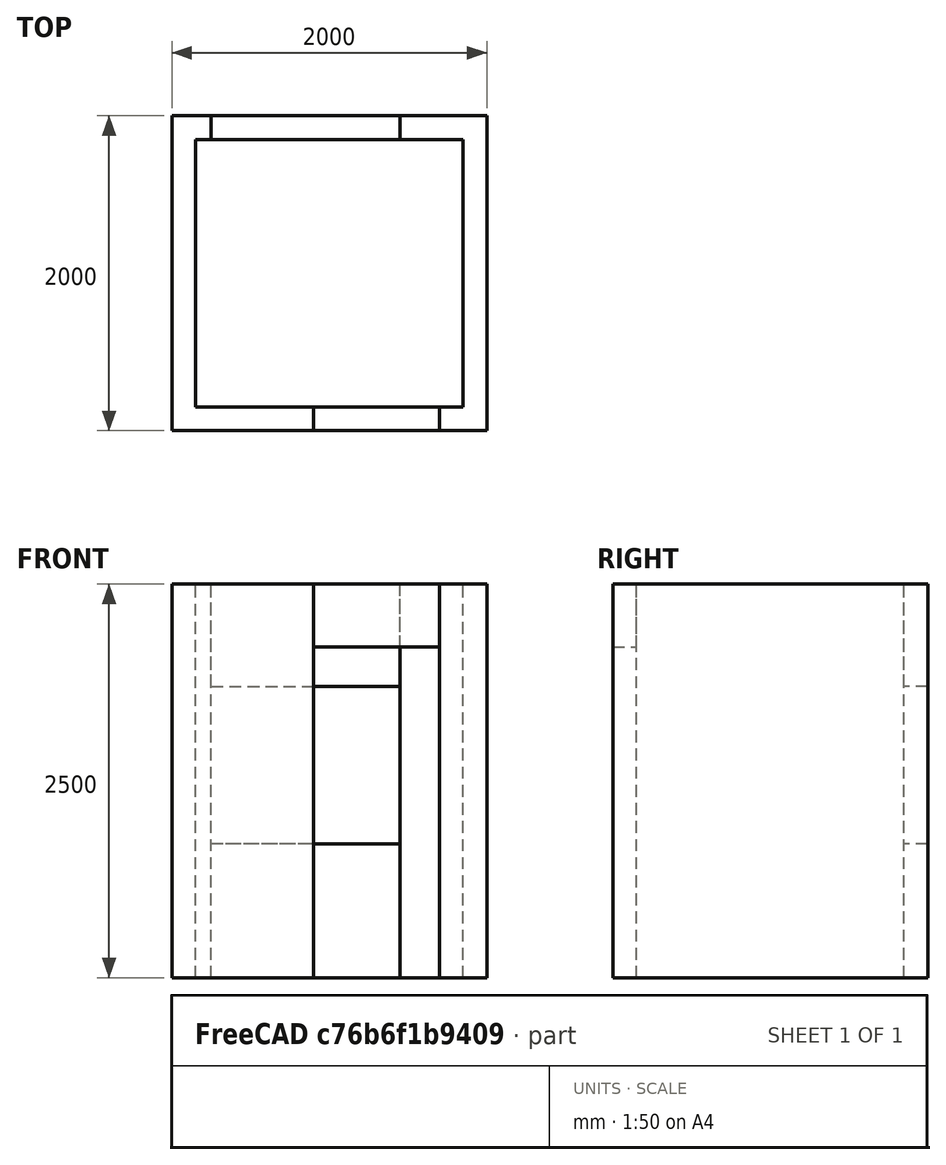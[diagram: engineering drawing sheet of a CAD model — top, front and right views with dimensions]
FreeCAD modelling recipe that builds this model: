
FCSTD DOCUMENT  (FreeCAD 0.17R13519 (Git))
Label: test007_draft
License: All rights reserved
LicenseURL: http://en.wikipedia.org/wiki/All_rights_reserved
objects: Part::Feature×80, Part::Part2DObjectPython×23, App::FeaturePython×10, App::DocumentObjectGroup×8, Part::Extrusion×7, Part::Cut×2
note: 112 computed .brp shape members not serialized (recipe doc carries the construction recipe); baked Part::Feature solids carry a one-line shape summary decoded from their .brp

FEATURE [Part::Part2DObjectPython] Rectangle  # Draft 2D object (typed FeaturePython)
  ChamferSize = 0
  Columns = 1
  FilletRadius = 0
  Height = 2000
  Length = 2000
  MakeFace = false
  Rows = 1
FEATURE [Part::Part2DObjectPython] Rectangle001  # Draft 2D object (typed FeaturePython)
  ChamferSize = 0
  Columns = 1
  FilletRadius = 0
  Height = 1700
  Length = 1700
  MakeFace = false
  Placement = pos=(150,150,0) rot=(0,0,1;0rad)
  Rows = 1
FEATURE [Part::Part2DObjectPython] Line  # Draft 2D object (typed FeaturePython)
  ChamferSize = 0
  Closed = false
  End = (150,3000,0)
  FilletRadius = 0
  Length = 2000
  MakeFace = true
  Points = (2) [(150,1000,0),(150,3000,0)]
  Start = (150,1000,0)
  Subdivisions = 0
FEATURE [Part::Part2DObjectPython] Line001  # Draft 2D object (typed FeaturePython)
  ChamferSize = 0
  Closed = false
  End = (250,3000,0)
  FilletRadius = 0
  Length = 2000
  MakeFace = true
  Placement = pos=(100,0,0) rot=(0,0,1;0rad)
  Points = (2) [(150,1000,0),(150,3000,0)]
  Start = (250,1000,0)
  Subdivisions = 0
FEATURE [Part::Part2DObjectPython] Line002  # Draft 2D object (typed FeaturePython)
  ChamferSize = 0
  Closed = false
  End = (1450,3000,0)
  FilletRadius = 0
  Length = 2000
  MakeFace = true
  Placement = pos=(1300,0,0) rot=(0,0,1;0rad)
  Points = (2) [(150,1000,0),(150,3000,0)]
  Start = (1450,1000,0)
  Subdivisions = 0
FEATURE [Part::Part2DObjectPython] Line003  # Draft 2D object (typed FeaturePython)
  ChamferSize = 0
  Closed = false
  End = (900,1000,0)
  FilletRadius = 0
  Length = 2000
  MakeFace = true
  Placement = pos=(750,-2000,0) rot=(0,0,1;0rad)
  Points = (2) [(150,1000,0),(150,3000,0)]
  Start = (900,-1000,0)
  Subdivisions = 0
FEATURE [Part::Part2DObjectPython] Line004  # Draft 2D object (typed FeaturePython)
  ChamferSize = 0
  Closed = false
  End = (1700,1000,0)
  FilletRadius = 0
  Length = 2000
  MakeFace = true
  Placement = pos=(1550,-2000,0) rot=(0,0,1;0rad)
  Points = (2) [(150,1000,0),(150,3000,0)]
  Start = (1700,-1000,0)
  Subdivisions = 0
FEATURE [Part::Part2DObjectPython] Line005  # Draft 2D object (typed FeaturePython)
  ChamferSize = 0
  Closed = false
  End = (1850,1000,0)
  FilletRadius = 0
  Length = 2000
  MakeFace = true
  Placement = pos=(1700,-2000,0) rot=(0,0,1;0rad)
  Points = (2) [(150,1000,0),(150,3000,0)]
  Start = (1850,-1000,0)
  Subdivisions = 0
FEATURE [Part::Part2DObjectPython] DWire  # Draft 2D object (typed FeaturePython)
  ChamferSize = 0
  Closed = true
  End = (250,2000,0)
  FilletRadius = 0
  Length = 6000
  MakeFace = true
  Points = (8) [(250,1850,0),(150,1850,0),(150,150,0),(900,150,0),(900,2.75546e-14,0),(1.26218e-29,3.8643e-46,0),(-6.12323e-14,2000,0),(250,2000,0)]
  Start = (250,1850,0)
  Subdivisions = 0
FEATURE [Part::Part2DObjectPython] DWire001  # Draft 2D object (typed FeaturePython)
  ChamferSize = 0
  Closed = true
  End = (1850,150,0)
  FilletRadius = 0
  Length = 5400
  MakeFace = true
  Points = (8) [(1700,150,0),(1700,0,0),(2000,6.1e-14,0),(2000,2000,0),(1450,2000,0),(1450,1850,0),(1850,1850,0),(1850,150,0)]
  Start = (1700,150,0)
  Subdivisions = 0
FEATURE [Part::Part2DObjectPython] Line006  # Draft 2D object (typed FeaturePython)
  ChamferSize = 0
  Closed = false
  End = (1450,1925,0)
  FilletRadius = 0
  Length = 1200
  MakeFace = false
  Points = (2) [(250,1925,0),(1450,1925,0)]
  Start = (250,1925,0)
  Subdivisions = 0
FEATURE [Part::Part2DObjectPython] Line009  # Draft 2D object (typed FeaturePython)
  ChamferSize = 0
  Closed = false
  End = (250,2000,0)
  FilletRadius = 0
  Length = 1200
  MakeFace = false
  Points = (2) [(1450,2000,0),(250,2000,0)]
  Start = (1450,2000,0)
  Subdivisions = 0
FEATURE [Part::Part2DObjectPython] Line011  # Draft 2D object (typed FeaturePython)
  ChamferSize = 0
  Closed = false
  End = (1450,1850,0)
  FilletRadius = 0
  Length = 1200
  MakeFace = false
  Points = (2) [(250,1850,0),(1450,1850,0)]
  Start = (250,1850,0)
  Subdivisions = 0
FEATURE [Part::Part2DObjectPython] Line013  # Draft 2D object (typed FeaturePython)
  ChamferSize = 0
  Closed = false
  End = (1700,150,0)
  FilletRadius = 0
  Length = 800
  MakeFace = false
  Points = (2) [(900,150,0),(1700,150,0)]
  Start = (900,150,0)
  Subdivisions = 0
FEATURE [Part::Part2DObjectPython] Line015  # Draft 2D object (typed FeaturePython)
  ChamferSize = 0
  Closed = false
  End = (1695.52,871.443,0)
  FilletRadius = 0
  Length = 800
  MakeFace = false
  Placement = pos=(1620.52,1771.44,0) rot=(0,0,-1;1.5708rad)
  Points = (2) [(1700,75,0),(900,75,0)]
  Start = (1695.52,71.4434,0)
  Subdivisions = 0
FEATURE [Part::Part2DObjectPython] Line019  # Draft 2D object (typed FeaturePython)
  ChamferSize = 0
  Closed = false
  End = (900,0,0)
  FilletRadius = 0
  Length = 800
  MakeFace = false
  Points = (2) [(1700,0,0),(900,2.8e-14,0)]
  Start = (1700,0,0)
  Subdivisions = 0
FEATURE [Part::Part2DObjectPython] Arc  # Draft 2D object (typed FeaturePython)
  FirstAngle = 90.3221
  LastAngle = 174.435
  MakeFace = false
  Placement = pos=(1700,75,0) rot=(0,0,1;0rad)
  Radius = 796.456
FEATURE [Part::Part2DObjectPython] Rectangle002  # Draft 2D object (typed FeaturePython)
  ChamferSize = 0
  Columns = 1
  FilletRadius = 0
  Height = 600
  Length = 1700
  MakeFace = false
  Placement = pos=(150,1250,800) rot=(0,0,1;0rad)
  Rows = 1
FEATURE [Part::Feature] Shape
  Placement = pos=(-6227.42,-15812.2,800) rot=(0,0,1;0rad)
  shape: bbox 182.6 x 182.6 x 2e-07 mm, 0 faces, 0 solids (baked)
FEATURE [Part::Feature] Shape001
  Placement = pos=(-6227.42,-15812.2,800) rot=(0,0,1;0rad)
  shape: bbox 2e-07 x 40.64 x 2e-07 mm, 0 faces, 0 solids (baked)
FEATURE [Part::Feature] Shape002
  Placement = pos=(-6227.42,-15812.2,800) rot=(0,0,1;0rad)
  shape: bbox 162.6 x 162.6 x 2e-07 mm, 0 faces, 0 solids (baked)
FEATURE [Part::Feature] Shape003
  Placement = pos=(-6227.42,-15812.2,800) rot=(0,0,1;0rad)
  shape: bbox 2e-07 x 600 x 2e-07 mm, 0 faces, 0 solids (baked)
FEATURE [Part::Feature] Shape004
  Placement = pos=(-6227.42,-15812.2,800) rot=(0,0,1;0rad)
  shape: bbox 2e-07 x 600 x 2e-07 mm, 0 faces, 0 solids (baked)
FEATURE [Part::Feature] Shape005
  Placement = pos=(-6227.42,-15812.2,800) rot=(0,0,1;0rad)
  shape: bbox 2e-07 x 600 x 2e-07 mm, 0 faces, 0 solids (baked)
FEATURE [Part::Feature] Shape006
  Placement = pos=(-6227.42,-15812.2,800) rot=(0,0,1;0rad)
  shape: bbox 150 x 150 x 2e-07 mm, 0 faces, 0 solids (baked)
FEATURE [Part::Feature] Shape007
  Placement = pos=(-6227.42,-15812.2,800) rot=(0,0,1;0rad)
  shape: bbox 182.6 x 182.6 x 2e-07 mm, 0 faces, 0 solids (baked)
FEATURE [Part::Feature] Shape008
  Placement = pos=(-6227.42,-15812.2,800) rot=(0,0,1;0rad)
  shape: bbox 2e-07 x 32.51 x 2e-07 mm, 0 faces, 0 solids (baked)
FEATURE [Part::Feature] Shape009
  Placement = pos=(-6227.42,-15812.2,800) rot=(0,0,1;0rad)
  shape: bbox 2e-07 x 40.64 x 2e-07 mm, 0 faces, 0 solids (baked)
FEATURE [Part::Feature] Shape010
  Placement = pos=(-6227.42,-15812.2,800) rot=(0,0,1;0rad)
  shape: bbox 32.51 x 2e-07 x 2e-07 mm, 0 faces, 0 solids (baked)
FEATURE [Part::Feature] Shape011
  Placement = pos=(-6227.42,-15812.2,800) rot=(0,0,1;0rad)
  shape: bbox 40.64 x 2e-07 x 2e-07 mm, 0 faces, 0 solids (baked)
FEATURE [Part::Feature] Shape012
  Placement = pos=(-6227.42,-15812.2,800) rot=(0,0,1;0rad)
  shape: bbox 40.64 x 2e-07 x 2e-07 mm, 0 faces, 0 solids (baked)
FEATURE [Part::Feature] Shape013
  Placement = pos=(-6227.42,-15812.2,800) rot=(0,0,1;0rad)
  shape: bbox 130 x 130 x 2e-07 mm, 0 faces, 0 solids (baked)
FEATURE [Part::Feature] Shape014
  Placement = pos=(-6227.42,-15812.2,800) rot=(0,0,1;0rad)
  shape: bbox 2e-07 x 32.51 x 2e-07 mm, 0 faces, 0 solids (baked)
FEATURE [Part::Feature] Shape015
  Placement = pos=(-6227.42,-15812.2,800) rot=(0,0,1;0rad)
  shape: bbox 32.51 x 2e-07 x 2e-07 mm, 0 faces, 0 solids (baked)
FEATURE [Part::Feature] Shape016
  Placement = pos=(-6227.42,-15812.2,800) rot=(0,0,1;0rad)
  shape: bbox 162.6 x 162.6 x 2e-07 mm, 0 faces, 0 solids (baked)
FEATURE [Part::Feature] Shape017
  Placement = pos=(-6227.42,-15812.2,800) rot=(0,0,1;0rad)
  shape: bbox 2e-07 x 40.64 x 2e-07 mm, 0 faces, 0 solids (baked)
FEATURE [Part::Feature] Shape018
  Placement = pos=(-6227.42,-15812.2,800) rot=(0,0,1;0rad)
  shape: bbox 500 x 2e-07 x 2e-07 mm, 0 faces, 0 solids (baked)
FEATURE [Part::Feature] Shape019
  Placement = pos=(-6227.42,-15812.2,800) rot=(0,0,1;0rad)
  shape: bbox 150 x 150 x 2e-07 mm, 0 faces, 0 solids (baked)
FEATURE [Part::Feature] Shape020 .. Shape023  x4 (patterned run collapsed; names and placements below)
  shape: bbox 41.11 x 41.11 x 2e-07 mm, 0 faces, 0 solids (baked)
  placements: all 4 at pos=(-6227.42,-15812.2,800) rot=(0,0,1;0rad)
FEATURE [Part::Feature] Shape024
  Placement = pos=(-6227.42,-15812.2,800) rot=(0,0,1;0rad)
  shape: bbox 21.21 x 21.21 x 2e-07 mm, 0 faces, 0 solids (baked)
FEATURE [Part::Feature] Shape025
  Placement = pos=(-6227.42,-15812.2,800) rot=(0,0,1;0rad)
  shape: bbox 5.657 x 5.657 x 2e-07 mm, 0 faces, 0 solids (baked)
FEATURE [Part::Feature] Shape026
  Placement = pos=(-6227.42,-15812.2,800) rot=(0,0,1;0rad)
  shape: bbox 21.21 x 21.21 x 2e-07 mm, 0 faces, 0 solids (baked)
FEATURE [Part::Feature] Shape027
  Placement = pos=(-6227.42,-15812.2,800) rot=(0,0,1;0rad)
  shape: bbox 5.657 x 5.657 x 2e-07 mm, 0 faces, 0 solids (baked)
FEATURE [Part::Feature] Shape028
  Placement = pos=(-6227.42,-15812.2,800) rot=(0,0,1;0rad)
  shape: bbox 21.21 x 21.21 x 2e-07 mm, 0 faces, 0 solids (baked)
FEATURE [Part::Feature] Shape029
  Placement = pos=(-6227.42,-15812.2,800) rot=(0,0,1;0rad)
  shape: bbox 5.657 x 5.657 x 2e-07 mm, 0 faces, 0 solids (baked)
FEATURE [Part::Feature] Shape030
  Placement = pos=(-6227.42,-15812.2,800) rot=(0,0,1;0rad)
  shape: bbox 21.21 x 21.21 x 2e-07 mm, 0 faces, 0 solids (baked)
FEATURE [Part::Feature] Shape031
  Placement = pos=(-6227.42,-15812.2,800) rot=(0,0,1;0rad)
  shape: bbox 5.657 x 5.657 x 2e-07 mm, 0 faces, 0 solids (baked)
FEATURE [Part::Feature] Shape032
  Placement = pos=(-6227.42,-15812.2,800) rot=(0,0,1;0rad)
  shape: bbox 21.21 x 21.21 x 2e-07 mm, 0 faces, 0 solids (baked)
FEATURE [Part::Feature] Shape033
  Placement = pos=(-6227.42,-15812.2,800) rot=(0,0,1;0rad)
  shape: bbox 5.657 x 5.657 x 2e-07 mm, 0 faces, 0 solids (baked)
FEATURE [Part::Feature] Shape034
  Placement = pos=(-6227.42,-15812.2,800) rot=(0,0,1;0rad)
  shape: bbox 21.21 x 21.21 x 2e-07 mm, 0 faces, 0 solids (baked)
FEATURE [Part::Feature] Shape035
  Placement = pos=(-6227.42,-15812.2,800) rot=(0,0,1;0rad)
  shape: bbox 5.657 x 5.657 x 2e-07 mm, 0 faces, 0 solids (baked)
FEATURE [Part::Feature] Shape036
  Placement = pos=(-6227.42,-15812.2,800) rot=(0,0,1;0rad)
  shape: bbox 21.21 x 21.21 x 2e-07 mm, 0 faces, 0 solids (baked)
FEATURE [Part::Feature] Shape037
  Placement = pos=(-6227.42,-15812.2,800) rot=(0,0,1;0rad)
  shape: bbox 5.657 x 5.657 x 2e-07 mm, 0 faces, 0 solids (baked)
FEATURE [Part::Feature] Shape038
  Placement = pos=(-6227.42,-15812.2,800) rot=(0,0,1;0rad)
  shape: bbox 21.21 x 21.21 x 2e-07 mm, 0 faces, 0 solids (baked)
FEATURE [Part::Feature] Shape039
  Placement = pos=(-6227.42,-15812.2,800) rot=(0,0,1;0rad)
  shape: bbox 5.657 x 5.657 x 2e-07 mm, 0 faces, 0 solids (baked)
FEATURE [Part::Feature] Shape040
  Placement = pos=(-6227.42,-15812.2,800) rot=(0,0,1;0rad)
  shape: bbox 500 x 2e-07 x 2e-07 mm, 0 faces, 0 solids (baked)
FEATURE [Part::Feature] Shape041
  Placement = pos=(-6227.42,-15812.2,800) rot=(0,0,1;0rad)
  shape: bbox 40.64 x 2e-07 x 2e-07 mm, 0 faces, 0 solids (baked)
FEATURE [Part::Feature] Shape042
  Placement = pos=(-6227.42,-15812.2,800) rot=(0,0,1;0rad)
  shape: bbox 40.64 x 2e-07 x 2e-07 mm, 0 faces, 0 solids (baked)
FEATURE [Part::Feature] Shape043
  Placement = pos=(-6227.42,-15812.2,800) rot=(0,0,1;0rad)
  shape: bbox 32.51 x 2e-07 x 2e-07 mm, 0 faces, 0 solids (baked)
FEATURE [Part::Feature] Shape044
  Placement = pos=(-6227.42,-15812.2,800) rot=(0,0,1;0rad)
  shape: bbox 2e-07 x 32.51 x 2e-07 mm, 0 faces, 0 solids (baked)
FEATURE [Part::Feature] Shape045
  Placement = pos=(-6227.42,-15812.2,800) rot=(0,0,1;0rad)
  shape: bbox 32.51 x 2e-07 x 2e-07 mm, 0 faces, 0 solids (baked)
FEATURE [Part::Feature] Shape046
  Placement = pos=(-6227.42,-15812.2,800) rot=(0,0,1;0rad)
  shape: bbox 2e-07 x 40.64 x 2e-07 mm, 0 faces, 0 solids (baked)
FEATURE [Part::Feature] Shape047
  Placement = pos=(-6227.42,-15812.2,800) rot=(0,0,1;0rad)
  shape: bbox 130 x 130 x 2e-07 mm, 0 faces, 0 solids (baked)
FEATURE [Part::Feature] Shape048
  Placement = pos=(-6227.42,-15812.2,800) rot=(0,0,1;0rad)
  shape: bbox 2e-07 x 32.51 x 2e-07 mm, 0 faces, 0 solids (baked)
FEATURE [Part::Feature] Shape049
  Placement = pos=(-6227.42,-15812.2,800) rot=(0,0,1;0rad)
  shape: bbox 487.7 x 2e-07 x 2e-07 mm, 0 faces, 0 solids (baked)
FEATURE [Part::Feature] Shape050
  Placement = pos=(-6227.42,-15812.2,800) rot=(0,0,1;0rad)
  shape: bbox 500 x 2e-07 x 2e-07 mm, 0 faces, 0 solids (baked)
FEATURE [Part::Feature] Shape051
  Placement = pos=(-6227.42,-15812.2,800) rot=(0,0,1;0rad)
  shape: bbox 500 x 2e-07 x 2e-07 mm, 0 faces, 0 solids (baked)
FEATURE [Part::Feature] Shape052
  Placement = pos=(-18263.6,-3835.18,800) rot=(0,0,1;0rad)
  shape: bbox 140.1 x 2e-07 x 2e-07 mm, 0 faces, 0 solids (baked)
FEATURE [Part::Feature] Shape053
  Placement = pos=(-18263.6,-3835.18,800) rot=(0,0,1;0rad)
  shape: bbox 2e-07 x 115.3 x 2e-07 mm, 0 faces, 0 solids (baked)
FEATURE [Part::Feature] Shape054
  Placement = pos=(-18263.6,-3835.18,800) rot=(0,0,1;0rad)
  shape: bbox 20 x 2e-07 x 2e-07 mm, 0 faces, 0 solids (baked)
FEATURE [Part::Feature] Shape055
  Placement = pos=(-18263.6,-3835.18,800) rot=(0,0,1;0rad)
  shape: bbox 2e-07 x 109.6 x 2e-07 mm, 0 faces, 0 solids (baked)
FEATURE [Part::Feature] Shape056
  Placement = pos=(-18263.6,-3835.18,800) rot=(0,0,1;0rad)
  shape: bbox 2e-07 x 5.643 x 2e-07 mm, 0 faces, 0 solids (baked)
FEATURE [Part::Feature] Shape057
  Placement = pos=(-18263.6,-3835.18,800) rot=(0,0,1;0rad)
  shape: bbox 20 x 2e-07 x 2e-07 mm, 0 faces, 0 solids (baked)
FEATURE [Part::Feature] Shape058
  Placement = pos=(-18263.6,-3835.18,800) rot=(0,0,1;0rad)
  shape: bbox 50 x 50 x 2e-07 mm, 0 faces, 0 solids (baked)
FEATURE [Part::Feature] Shape059 .. Shape064  x6 (patterned run collapsed; names and placements below)
  shape: bbox 299.7 x 2e-07 x 2e-07 mm, 0 faces, 0 solids (baked)
  placements: all 6 at pos=(-18263.6,-3835.18,800) rot=(0,0,1;0rad)
FEATURE [Part::Feature] Shape065
  Placement = pos=(-18263.6,-3835.18,800) rot=(0,0,1;0rad)
  shape: bbox 50 x 50 x 2e-07 mm, 0 faces, 0 solids (baked)
FEATURE [Part::Feature] Shape067
  Placement = pos=(-18263.6,-3835.18,800) rot=(0,0,1;0rad)
  shape: bbox 50 x 50 x 2e-07 mm, 0 faces, 0 solids (baked)
FEATURE [Part::Feature] Shape068
  Placement = pos=(-18263.6,-3835.18,800) rot=(0,0,1;0rad)
  shape: bbox 50 x 50 x 2e-07 mm, 0 faces, 0 solids (baked)
FEATURE [Part::Feature] Shape069
  Placement = pos=(-18263.6,-3835.18,800) rot=(0,0,1;0rad)
  shape: bbox 300 x 2e-07 x 2e-07 mm, 0 faces, 0 solids (baked)
FEATURE [Part::Feature] Shape070
  Placement = pos=(-18263.6,-3835.18,800) rot=(0,0,1;0rad)
  shape: bbox 299.7 x 2e-07 x 2e-07 mm, 0 faces, 0 solids (baked)
FEATURE [Part::Feature] Shape072
  Placement = pos=(-18263.6,-3835.18,800) rot=(0,0,1;0rad)
  shape: bbox 140 x 2e-07 x 2e-07 mm, 0 faces, 0 solids (baked)
FEATURE [Part::Feature] Shape073
  Placement = pos=(-18263.6,-3835.18,800) rot=(0,0,1;0rad)
  shape: bbox 299.7 x 2e-07 x 2e-07 mm, 0 faces, 0 solids (baked)
FEATURE [Part::Feature] Shape074
  Placement = pos=(-18263.6,-3835.18,800) rot=(0,0,1;0rad)
  shape: bbox 2e-07 x 250 x 2e-07 mm, 0 faces, 0 solids (baked)
FEATURE [Part::Feature] Shape075
  Placement = pos=(-18263.6,-3835.18,800) rot=(0,0,1;0rad)
  shape: bbox 850 x 2e-07 x 2e-07 mm, 0 faces, 0 solids (baked)
FEATURE [Part::Feature] Shape076
  Placement = pos=(-18263.6,-3835.18,800) rot=(0,0,1;0rad)
  shape: bbox 2e-07 x 500 x 2e-07 mm, 0 faces, 0 solids (baked)
FEATURE [Part::Feature] Shape077
  Placement = pos=(-18263.6,-3835.18,800) rot=(0,0,1;0rad)
  shape: bbox 850 x 2e-07 x 2e-07 mm, 0 faces, 0 solids (baked)
FEATURE [Part::Feature] Shape078
  Placement = pos=(-18263.6,-3835.18,800) rot=(0,0,1;0rad)
  shape: bbox 2e-07 x 500 x 2e-07 mm, 0 faces, 0 solids (baked)
FEATURE [Part::Feature] Shape079
  Placement = pos=(-18263.6,-3835.18,800) rot=(0,0,1;0rad)
  shape: bbox 850 x 2e-07 x 2e-07 mm, 0 faces, 0 solids (baked)
FEATURE [Part::Part2DObjectPython] Line020  # Draft 2D object (typed FeaturePython)
  ChamferSize = 0
  Closed = false
  End = (150,1250,0)
  FilletRadius = 0
  Length = 1209.34
  MakeFace = false
  Points = (2) [(1200,1850,0),(150,1250,0)]
  Start = (1200,1850,0)
  Subdivisions = 0
  Support = -> [Rectangle002]
FEATURE [App::DocumentObjectGroup] Construction
  Group = -> [Rectangle,Rectangle001,Line,Line001,Line002,Line003,Line004,Line005,Line020]
FEATURE [App::FeaturePython] Dimension001  # Draft dimension (typed FeaturePython)
  Diameter = false
  Dimline = (2200,0,0)
  Direction = (0,0,0)
  Distance = 2000
  End = (2000,0,0)
  Normal = (0,0,1)
  Start = (2000,2000,0)
FEATURE [App::FeaturePython] Dimension  # Draft dimension (typed FeaturePython)
  Diameter = false
  Dimline = (1000,2200,0)
  Direction = (0,0,0)
  Distance = 1200
  End = (1450,2000,0)
  Normal = (0,0,1)
  Start = (250,2000,0)
FEATURE [App::FeaturePython] Dimension002  # Draft dimension (typed FeaturePython)
  Diameter = false
  Dimline = (100,2200,0)
  Direction = (0,0,0)
  Distance = 250
  End = (250,2000,0)
  Normal = (0,0,1)
  Start = (0,2000,0)
FEATURE [App::FeaturePython] Dimension003  # Draft dimension (typed FeaturePython)
  Diameter = false
  Dimline = (1700,2200,0)
  Direction = (0,0,0)
  Distance = 550
  End = (2000,2000,0)
  Normal = (0,0,1)
  Start = (1450,2000,0)
FEATURE [App::FeaturePython] Dimension004  # Draft dimension (typed FeaturePython)
  Diameter = false
  Dimline = (-200,100,0)
  Direction = (0,0,0)
  Distance = 2000
  End = (0,0,0)
  Normal = (0,0,1)
  Start = (0,2000,0)
FEATURE [App::FeaturePython] Dimension005  # Draft dimension (typed FeaturePython)
  Diameter = false
  Dimline = (900,-200,0)
  Direction = (0,0,0)
  Distance = 900
  End = (900,0,0)
  Normal = (0,0,1)
  Start = (0,0,0)
FEATURE [App::FeaturePython] Dimension006  # Draft dimension (typed FeaturePython)
  Diameter = false
  Dimline = (1600,-200,0)
  Direction = (0,0,0)
  Distance = 800
  End = (1700,0,0)
  Normal = (0,0,1)
  Start = (900,0,0)
FEATURE [App::FeaturePython] Dimension007  # Draft dimension (typed FeaturePython)
  Diameter = false
  Dimline = (1900,-200,0)
  Direction = (0,0,0)
  Distance = 300
  End = (2000,0,0)
  Normal = (0,0,1)
  Start = (1700,0,0)
FEATURE [App::FeaturePython] Dimension008  # Draft dimension (typed FeaturePython)
  Diameter = false
  Dimline = (100,2100,0)
  Direction = (0,0,0)
  Distance = 150
  End = (0,1850,0)
  Normal = (0,0,1)
  Start = (150,1850,0)
FEATURE [App::FeaturePython] Dimension009  # Draft dimension (typed FeaturePython)
  Diameter = false
  Dimline = (-100,1900,0)
  Direction = (0,0,0)
  Distance = 150
  End = (150,2000,0)
  Normal = (0,0,1)
  Start = (150,1850,0)
FEATURE [App::DocumentObjectGroup] Group001  label="labels"
  Group = -> [Dimension001,Dimension,Dimension002,Dimension003,Dimension004,Dimension005,Dimension006,Dimension007,Dimension008,Dimension009]
FEATURE [Part::Part2DObjectPython] DWire002  # Draft 2D object (typed FeaturePython)
  ChamferSize = 0
  Closed = true
  End = (250,1850,0)
  FilletRadius = 0
  Length = 2700
  MakeFace = true
  Points = (4) [(250,2000,0),(1450,2000,0),(1450,1850,0),(250,1850,0)]
  Start = (250,2000,0)
  Subdivisions = 0
FEATURE [Part::Extrusion] Extrude001
  Base = -> DWire001
  Dir = (0,0,1)
  DirMode = 2
  FaceMakerClass = Part::FaceMakerBullseye
  LengthFwd = 2500
  LengthRev = 0
  Solid = false
  Symmetric = false
FEATURE [Part::Extrusion] Extrude003
  Base = -> DWire
  Dir = (0,0,1)
  DirMode = 2
  FaceMakerClass = Part::FaceMakerBullseye
  LengthFwd = 2500
  LengthRev = 0
  Solid = false
  Symmetric = false
FEATURE [Part::Extrusion] Extrude002
  Base = -> DWire002
  Dir = (0,0,1)
  DirMode = 2
  FaceMakerClass = Part::FaceMakerBullseye
  LengthFwd = 2500
  LengthRev = 0
  Solid = false
  Symmetric = false
FEATURE [Part::Part2DObjectPython] DWire003  # Draft 2D object (typed FeaturePython)
  ChamferSize = 0
  Closed = true
  End = (1700,150,0)
  FilletRadius = 0
  Length = 1900
  MakeFace = false
  Points = (4) [(900,150,0),(900,2.8e-14,0),(1700,0,0),(1700,150,0)]
  Start = (900,150,0)
  Subdivisions = 0
FEATURE [App::DocumentObjectGroup] Group002  label="floor"
  Group = -> [DWire,DWire001,Line006,Line009,Line011,Line013,Line015,Line019,Arc,DWire002,DWire003]
FEATURE [Part::Extrusion] Extrude
  Base = -> DWire003
  Dir = (0,0,1)
  DirMode = 2
  FaceMakerClass = Part::FaceMakerBullseye
  LengthFwd = 2500
  LengthRev = 0
  Solid = true
  Symmetric = false
FEATURE [Part::Part2DObjectPython] Rectangle003  # Draft 2D object (typed FeaturePython)
  ChamferSize = 0
  Columns = 1
  FilletRadius = 0
  Height = 2100
  Length = 800
  MakeFace = false
  Placement = pos=(900,0,0) rot=(1,0,0;1.5708rad)
  Rows = 1
  Support = -> [Extrude]
FEATURE [Part::Extrusion] Extrude004
  Base = -> Rectangle003
  Dir = (0,-1,0)
  DirMode = 2
  FaceMakerClass = Part::FaceMakerBullseye
  LengthFwd = 150
  LengthRev = 0
  Reversed = true
  Solid = true
  Symmetric = false
FEATURE [Part::Cut] Cut
  Base = -> Extrude
  Tool = -> Extrude004
FEATURE [App::DocumentObjectGroup] Group003  label="door"
  Group = -> [Cut,Rectangle003]
FEATURE [Part::Part2DObjectPython] Rectangle004  # Draft 2D object (typed FeaturePython)
  ChamferSize = 0
  Columns = 1
  FilletRadius = 0
  Height = 1000
  Length = 1200
  MakeFace = false
  Placement = pos=(1450,2000,850) rot=(0,0.707107,0.707107;3.14159rad)
  Rows = 1
FEATURE [Part::Extrusion] Extrude005
  Base = -> Rectangle004
  Dir = (0,1,0)
  DirMode = 2
  FaceMakerClass = Part::FaceMakerBullseye
  LengthFwd = 150
  LengthRev = 0
  Reversed = true
  Solid = true
  Symmetric = false
FEATURE [Part::Cut] Cut001
  Base = -> Extrude002
  Tool = -> Extrude005
FEATURE [App::DocumentObjectGroup] Group004  label="window"
  Group = -> [Cut001,Rectangle004]
FEATURE [Part::Extrusion] Extrude006
  Base = -> Rectangle002
  Dir = (0,0,1)
  DirMode = 2
  FaceMakerClass = Part::FaceMakerBullseye
  LengthFwd = 100
  LengthRev = 0
  Reversed = true
  Solid = false
  Symmetric = false
FEATURE [Part::Feature] Shape071
  Placement = pos=(-18263.6,-3835.18,800) rot=(0,0,1;0rad)
  shape: bbox 2e-07 x 250 x 2e-07 mm, 0 faces, 0 solids (baked)
FEATURE [Part::Feature] Shape066
  Placement = pos=(-18263.6,-3835.18,800) rot=(0,0,1;0rad)
  shape: bbox 50 x 50 x 2e-07 mm, 0 faces, 0 solids (baked)
FEATURE [App::DocumentObjectGroup] Group  label="sink_cooktop"
  Group = -> [Shape,Shape001,Shape002,Shape003,Shape004,Shape005,Shape006,Shape007,Shape008,Shape009,Shape010,Shape011,Shape012,Shape013,Shape014,Shape015,Shape016,Shape017,Shape018,Shape019,Shape020,Shape021,Shape022,Shape023,Shape024,Shape025,Shape026,Shape027,Shape028,Shape029,Shape030,Shape031,Shape032,Shape033,Shape034,Shape035,Shape036,Shape037,Shape038,Shape039,Shape040,Shape041,Shape042,Shape043,+36 more]
FEATURE [App::DocumentObjectGroup] Group005  label="cooking_top"
  Group = -> [Group,Rectangle002,Extrude006]
FEATURE [App::DocumentObjectGroup] Group006  label="walls"
  Group = -> [Extrude001,Extrude003]
